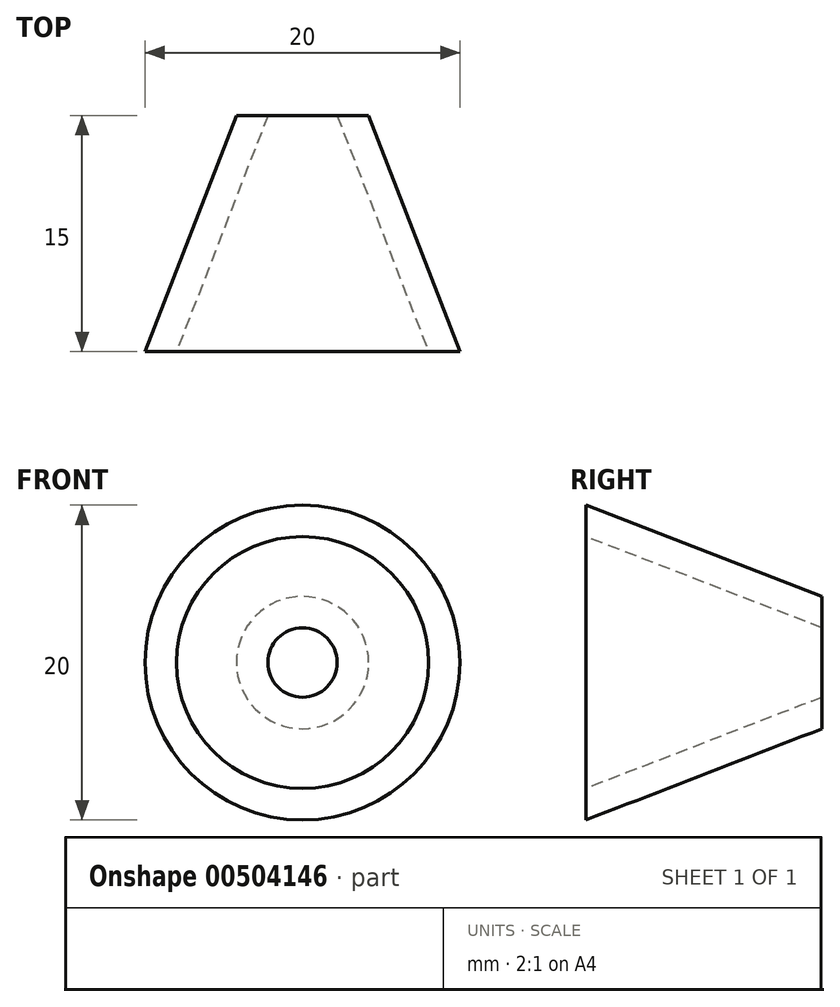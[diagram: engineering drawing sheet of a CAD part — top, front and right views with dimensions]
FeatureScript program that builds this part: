
annotation { "Feature Type Name" : "Feature", "Feature Type Description" : "" }
export const myFeature = defineFeature(function(context is Context, id is Id, definition is map)
    precondition{}
    {
        {
            var Q0;
            Q0=qCreatedBy(makeId("Top.planeOp"),FACE);
            var sketch = newSketch(context, id + "F0", { "sketchPlane" : qUnion([Q0])});
            skLineSegment(sketch, "E0", {"start": v(8, 0) * mm, "end": v(2.2, 15) * mm});
            skLineSegment(sketch, "E1", {"start": v(4.2, 15) * mm, "end": v(10, 0) * mm});
            skLineSegment(sketch, "E2", {"start": v(10, 0) * mm, "end": v(8, 0) * mm});
            skLineSegment(sketch, "E3", {"start": v(2.2, 15) * mm, "end": v(4.2, 15) * mm});
            skLineSegment(sketch, "E4", {"start": v(0, 0) * mm, "end": v(0, 15) * mm});
            skSolve(sketch);
        }
        {
            var Q0;
            Q0=makeQuery(id+"F0.imprint","IMPRINT",FACE,{"disambiguationData":[TD([[makeQuery(id+"F0.imprint","IMPRINT",EDGE,{"derivedFrom":sQuery(id+"F0.wireOp",EDGE,"E0")}),-1.0]])]});
            var Q1;
            Q1=sQuery(id+"F0.wireOp",EDGE,"E4");
            revolve(context, id + "F1", {"surfaceOperationType" : NewSurfaceOperationType.NEW, "entities" : qUnion([Q0]), "axis" : qUnion([Q1]), "revolveType" : RevolveType.FULL});
        }
    });
